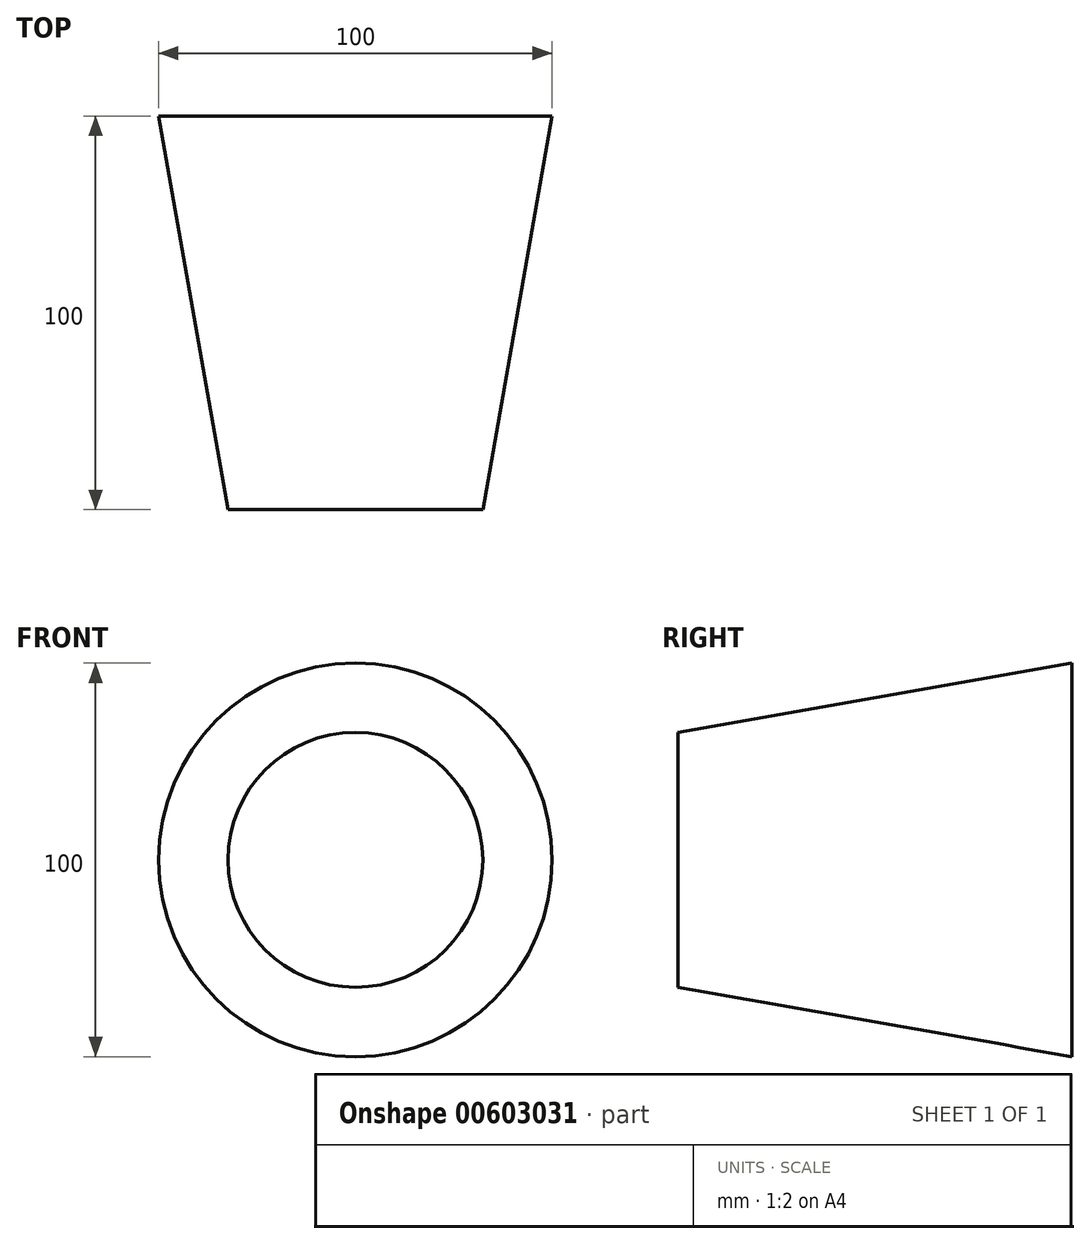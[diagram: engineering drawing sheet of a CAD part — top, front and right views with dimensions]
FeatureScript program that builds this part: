
annotation { "Feature Type Name" : "Feature", "Feature Type Description" : "" }
export const myFeature = defineFeature(function(context is Context, id is Id, definition is map)
    precondition{}
    {
        {
            var Q0;
            Q0=qCreatedBy(makeId("Front.planeOp"),FACE);
            var sketch = newSketch(context, id + "F0", { "sketchPlane" : qUnion([Q0])});
            skCircle(sketch, "E0", {"center": v(0, 0) * mm, "radius": 50 * mm});
            skSolve(sketch);
        }
        {
            var Q0;
            Q0=makeQuery(id+"F0.imprint","IMPRINT",FACE,{"disambiguationData":[TD([[makeQuery(id+"F0.imprint","IMPRINT",EDGE,{"derivedFrom":sQuery(id+"F0.wireOp",EDGE,"E0")}),1.0]])]});
            extrude(context, id + "F1", {"entities" : qUnion([Q0]), "depth" : 100 * mm, "offsetDistance" : 25 * mm, "hasDraft" : true, "draftAngle" : 10 * degree, "draftPullDirection" : true});
        }
    });
